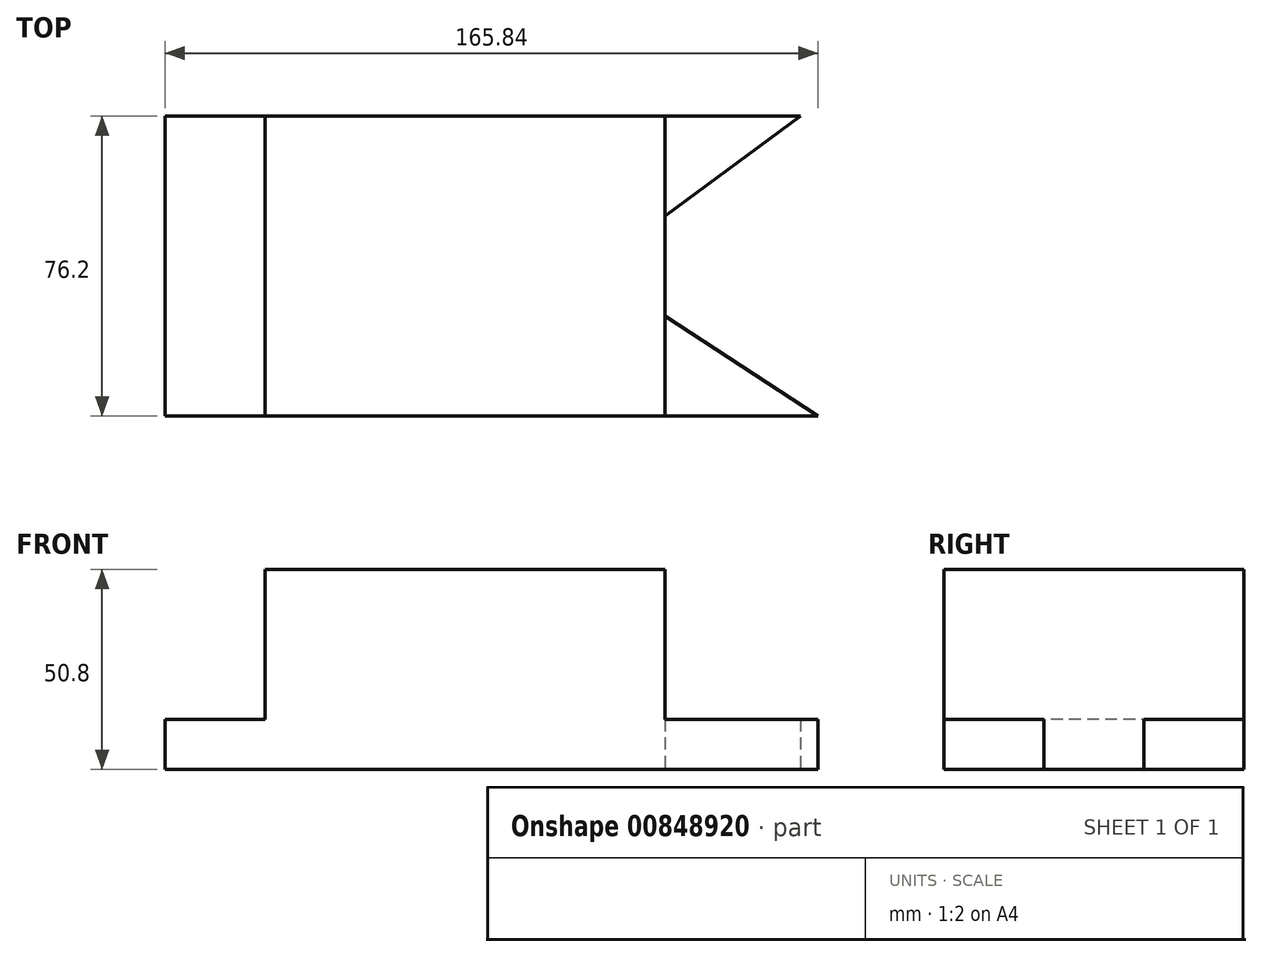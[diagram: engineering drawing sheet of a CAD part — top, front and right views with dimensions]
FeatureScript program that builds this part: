
annotation { "Feature Type Name" : "Feature", "Feature Type Description" : "" }
export const myFeature = defineFeature(function(context is Context, id is Id, definition is map)
    precondition{}
    {
        {
            var Q0;
            Q0=qCreatedBy(makeId("Top.planeOp"),FACE);
            var sketch = newSketch(context, id + "F0", { "sketchPlane" : qUnion([Q0])});
            skLineSegment(sketch, "E0.bottom", {"start": v(-37.53, 34.5) * mm, "end": v(-12.13, 34.5) * mm});
            skLineSegment(sketch, "E0.top", {"start": v(-37.53, -41.7) * mm, "end": v(-12.13, -41.7) * mm});
            skLineSegment(sketch, "E0.left", {"start": v(-37.53, 34.5) * mm, "end": v(-37.53, -41.7) * mm});
            skLineSegment(sketch, "E0.right", {"start": v(-12.13, 34.5) * mm, "end": v(-12.13, -41.7) * mm});
            skLineSegment(sketch, "E1.bottom", {"start": v(-12.13, 34.5) * mm, "end": v(89.47, 34.5) * mm});
            skLineSegment(sketch, "E1.top", {"start": v(-12.13, -41.7) * mm, "end": v(89.47, -41.7) * mm});
            skLineSegment(sketch, "E1.right", {"start": v(89.47, 34.5) * mm, "end": v(89.47, -41.7) * mm});
            skLineSegment(sketch, "E2", {"start": v(89.47, 34.5) * mm, "end": v(123.83, 34.5) * mm});
            skLineSegment(sketch, "E3", {"start": v(123.83, 34.5) * mm, "end": v(89.47, 9.1) * mm});
            skLineSegment(sketch, "E4", {"start": v(89.47, -41.7) * mm, "end": v(128.31, -41.7) * mm});
            skLineSegment(sketch, "E5", {"start": v(128.31, -41.7) * mm, "end": v(89.47, -16.3) * mm});
            skSolve(sketch);
        }
        {
            var Q0;
            Q0=makeQuery(id+"F0.imprint","IMPRINT",FACE,{"disambiguationData":[TD([[makeQuery(id+"F0.imprint","IMPRINT",EDGE,{"derivedFrom":sQuery(id+"F0.wireOp",EDGE,"E0.bottom")}),-1.0]])]});
            extrude(context, id + "F1", {"entities" : qUnion([Q0]), "depth" : 12.7 * mm, "offsetDistance" : 25.4 * mm});
        }
        {
            var Q0;
            {var subQ1=sQuery(id+"F0.wireOp",EDGE,"E1.bottom");Q0=makeQuery(id+"F0.imprint","IMPRINT",FACE,{"disambiguationData":[TD([[makeQuery(id+"F0.imprint","IMPRINT",EDGE,{"derivedFrom":subQ1}),-1.0]])]});}
            extrude(context, id + "F2", {"entities" : qUnion([Q0]), "operationType" : NewBodyOperationType.ADD, "depth" : 50.8 * mm, "offsetDistance" : 25.4 * mm});
        }
        {
            var Q0;
            {var subQ0=sQuery(id+"F0.wireOp",EDGE,"E2");Q0=makeQuery(id+"F0.imprint","IMPRINT",FACE,{"disambiguationData":[TD([[makeQuery(id+"F0.imprint","IMPRINT",EDGE,{"derivedFrom":subQ0}),-1.0]])]});}
            extrude(context, id + "F3", {"entities" : qUnion([Q0]), "operationType" : NewBodyOperationType.ADD, "depth" : 12.7 * mm, "offsetDistance" : 25.4 * mm});
        }
        {
            var Q0;
            {var subQ0=sQuery(id+"F0.wireOp",EDGE,"E4");Q0=makeQuery(id+"F0.imprint","IMPRINT",FACE,{"disambiguationData":[TD([[makeQuery(id+"F0.imprint","IMPRINT",EDGE,{"derivedFrom":subQ0}),1.0]])]});}
            extrude(context, id + "F4", {"entities" : qUnion([Q0]), "operationType" : NewBodyOperationType.ADD, "depth" : 12.7 * mm, "offsetDistance" : 25.4 * mm});
        }
    });
